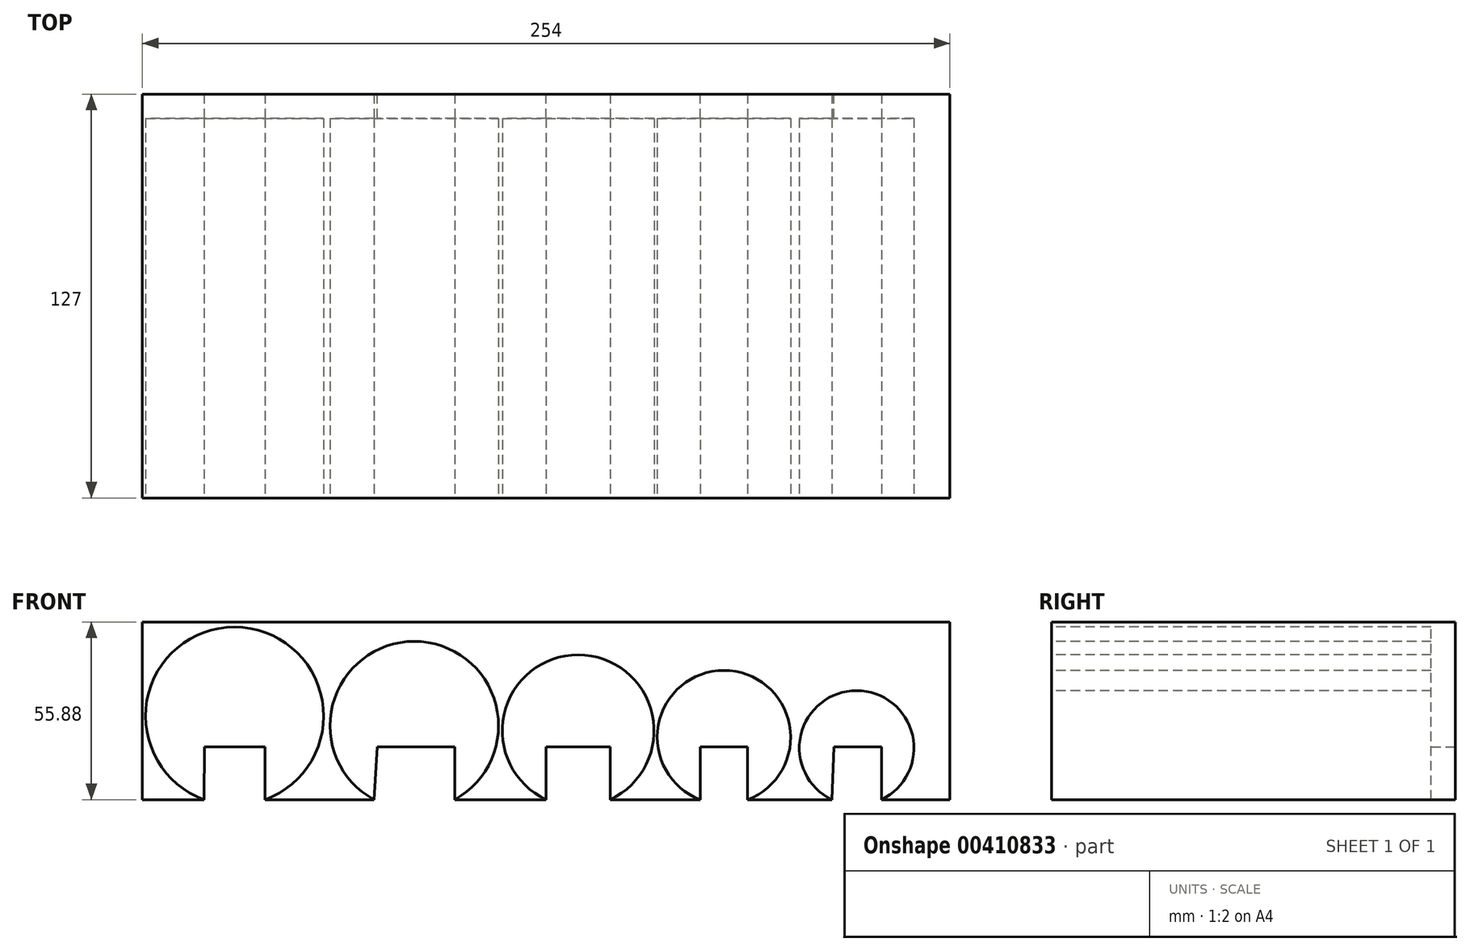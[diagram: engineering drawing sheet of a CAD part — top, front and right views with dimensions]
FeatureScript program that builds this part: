
annotation { "Feature Type Name" : "Feature", "Feature Type Description" : "" }
export const myFeature = defineFeature(function(context is Context, id is Id, definition is map)
    precondition{}
    {
        {
            var Q0;
            Q0=qCreatedBy(makeId("Front.planeOp"),FACE);
            var sketch = newSketch(context, id + "F0", { "sketchPlane" : qUnion([Q0])});
            skLineSegment(sketch, "E0.bottom", {"start": v(-127, 27.94) * mm, "end": v(127, 27.94) * mm});
            skLineSegment(sketch, "E0.top", {"start": v(-127, -27.94) * mm, "end": v(127, -27.94) * mm});
            skLineSegment(sketch, "E0.left", {"start": v(-127, 27.94) * mm, "end": v(-127, -27.94) * mm});
            skLineSegment(sketch, "E0.right", {"start": v(127, 27.94) * mm, "end": v(127, -27.94) * mm});
            skPoint(sketch, "E0.middle", {"position": v(0, 0) * mm});
            skSolve(sketch);
        }
        {
            var Q0;
            Q0=makeQuery(id+"F0.imprint","IMPRINT",FACE,{"disambiguationData":[TD([[makeQuery(id+"F0.imprint","IMPRINT",EDGE,{"derivedFrom":sQuery(id+"F0.wireOp",EDGE,"E0.bottom")}),-1.0]])]});
            extrude(context, id + "F1", {"entities" : qUnion([Q0]), "depth" : 127 * mm});
        }
        {
            var Q0;
            Q0=makeQuery(id+"F1.opExtrude","CAP_FACE",FACE,{"disambiguationData":[OSD([sQuery(id+"F0.wireOp",EDGE,"E0.bottom"),sQuery(id+"F0.wireOp",EDGE,"E0.top"),sQuery(id+"F0.wireOp",EDGE,"E0.left"),sQuery(id+"F0.wireOp",EDGE,"E0.right")])],"isStart":false});
            var sketch = newSketch(context, id + "F2", { "sketchPlane" : qUnion([Q0])});
            skArc(sketch, "E1", {"start": v(-88.41, -27.94) * mm, "mid": v(-98, 26.37) * mm, "end": v(-107.6, -27.94) * mm});
            skLineSegment(sketch, "E2.0", {"start": v(-127, -27.94) * mm, "end": v(127, -27.94) * mm});
            skSolve(sketch);
        }
        {
            var Q0;
            {var subQ2=sQuery(id+"F2.wireOp",EDGE,"E1");Q0=makeQuery(id+"F2.imprint","IMPRINT",FACE,{"disambiguationData":[TD([[makeQuery(id+"F2.imprint","IMPRINT",EDGE,{"derivedFrom":subQ2}),-1.0]])]});}
            var sketch = newSketch(context, id + "F3", { "sketchPlane" : qUnion([Q0])});
            skLineSegment(sketch, "E3.0", {"start": v(-127, -27.94) * mm, "end": v(127, -27.94) * mm});
            skArc(sketch, "E4", {"start": v(-28.8, -27.94) * mm, "mid": v(-41.48, 21.83) * mm, "end": v(-54.17, -27.94) * mm});
            skSolve(sketch);
        }
        {
            var Q0;
            {var subQ2=sQuery(id+"F2.wireOp",EDGE,"E1");Q0=makeQuery(id+"F2.imprint","IMPRINT",FACE,{"disambiguationData":[TD([[makeQuery(id+"F2.imprint","IMPRINT",EDGE,{"derivedFrom":subQ2}),-1.0]])]});}
            var sketch = newSketch(context, id + "F4", { "sketchPlane" : qUnion([Q0])});
            skLineSegment(sketch, "E5.0", {"start": v(-127, -27.94) * mm, "end": v(127, -27.94) * mm});
            skArc(sketch, "E6", {"start": v(20.14, -27.94) * mm, "mid": v(10.07, 17.6) * mm, "end": v(0, -27.94) * mm});
            skSolve(sketch);
        }
        {
            var Q0;
            {var subQ2=sQuery(id+"F2.wireOp",EDGE,"E1");Q0=makeQuery(id+"F2.imprint","IMPRINT",FACE,{"disambiguationData":[TD([[makeQuery(id+"F2.imprint","IMPRINT",EDGE,{"derivedFrom":subQ2}),-1.0]])]});}
            var sketch = newSketch(context, id + "F5", { "sketchPlane" : qUnion([Q0])});
            skLineSegment(sketch, "E7.0", {"start": v(-127, -27.94) * mm, "end": v(127, -27.94) * mm});
            skArc(sketch, "E8", {"start": v(63.36, -27.94) * mm, "mid": v(55.92, 12.7) * mm, "end": v(48.5, -27.94) * mm});
            skSolve(sketch);
        }
        {
            var Q0;
            {var subQ2=sQuery(id+"F2.wireOp",EDGE,"E1");Q0=makeQuery(id+"F2.imprint","IMPRINT",FACE,{"disambiguationData":[TD([[makeQuery(id+"F2.imprint","IMPRINT",EDGE,{"derivedFrom":subQ2}),-1.0]])]});}
            var sketch = newSketch(context, id + "F6", { "sketchPlane" : qUnion([Q0])});
            skLineSegment(sketch, "E9.0", {"start": v(-127, -27.94) * mm, "end": v(127, -27.94) * mm});
            skArc(sketch, "E10", {"start": v(105.44, -27.94) * mm, "mid": v(97.67, 6.36) * mm, "end": v(89.9, -27.94) * mm});
            skSolve(sketch);
        }
        {
            var Q0;
            {var subQ0=sQuery(id+"F6.wireOp",EDGE,"E10");Q0=makeQuery(id+"F6.imprint","IMPRINT",FACE,{"disambiguationData":[TD([[makeQuery(id+"F6.imprint","IMPRINT",EDGE,{"derivedFrom":subQ0}),1.0]])]});}
            extrude(context, id + "F7", {"entities" : qUnion([Q0]), "operationType" : NewBodyOperationType.REMOVE, "oppositeDirection" : true, "depth" : 251.46 * mm});
        }
        {
            var Q0;
            {var subQ0=sQuery(id+"F5.wireOp",EDGE,"E8");Q0=makeQuery(id+"F5.imprint","IMPRINT",FACE,{"disambiguationData":[TD([[makeQuery(id+"F5.imprint","IMPRINT",EDGE,{"derivedFrom":subQ0}),1.0]])]});}
            extrude(context, id + "F8", {"entities" : qUnion([Q0]), "operationType" : NewBodyOperationType.REMOVE, "oppositeDirection" : true, "depth" : 251.46 * mm});
        }
        {
            var Q0;
            {var subQ0=sQuery(id+"F4.wireOp",EDGE,"E6");Q0=makeQuery(id+"F4.imprint","IMPRINT",FACE,{"disambiguationData":[TD([[makeQuery(id+"F4.imprint","IMPRINT",EDGE,{"derivedFrom":subQ0}),1.0]])]});}
            extrude(context, id + "F9", {"entities" : qUnion([Q0]), "operationType" : NewBodyOperationType.REMOVE, "oppositeDirection" : true, "depth" : 251.46 * mm});
        }
        {
            var Q0;
            {var subQ0=sQuery(id+"F3.wireOp",EDGE,"E4");Q0=makeQuery(id+"F3.imprint","IMPRINT",FACE,{"disambiguationData":[TD([[makeQuery(id+"F3.imprint","IMPRINT",EDGE,{"derivedFrom":subQ0}),1.0]])]});}
            extrude(context, id + "F10", {"entities" : qUnion([Q0]), "operationType" : NewBodyOperationType.REMOVE, "oppositeDirection" : true, "depth" : 251.46 * mm});
        }
        {
            var Q0;
            {var subQ0=sQuery(id+"F2.wireOp",EDGE,"E1");Q0=makeQuery(id+"F2.imprint","IMPRINT",FACE,{"disambiguationData":[TD([[makeQuery(id+"F2.imprint","IMPRINT",EDGE,{"derivedFrom":subQ0}),1.0]])]});}
            extrude(context, id + "F11", {"entities" : qUnion([Q0]), "operationType" : NewBodyOperationType.REMOVE, "oppositeDirection" : true, "depth" : 251.46 * mm});
        }
        {
            var Q0;
            Q0=makeQuery(id+"F1.opExtrude","SWEPT_FACE",FACE,{"disambiguationData":[OSD([sQuery(id+"F0.wireOp",EDGE,"E0.top")])]});
            var sketch = newSketch(context, id + "F12", { "sketchPlane" : qUnion([Q0])});
            skLineSegment(sketch, "E11.0.0", {"start": v(-126, 127) * mm, "end": v(-70, 127) * mm});
            skLineSegment(sketch, "E11.0.1", {"start": v(-107.6, 127) * mm, "end": v(-107.6, 2.54) * mm});
            skLineSegment(sketch, "E11.0.2", {"start": v(-70, 2.54) * mm, "end": v(-126, 2.54) * mm});
            skLineSegment(sketch, "E11.0.3", {"start": v(-88.41, 2.54) * mm, "end": v(-88.41, 127) * mm});
            skLineSegment(sketch, "E12", {"start": v(-126, 4.34) * mm, "end": v(-70, 4.34) * mm});
            skLineSegment(sketch, "E13", {"start": v(-126, 2.54) * mm, "end": v(-126, 4.34) * mm});
            skLineSegment(sketch, "E14.0.0", {"start": v(79.64, 127) * mm, "end": v(115.7, 127) * mm});
            skLineSegment(sketch, "E14.0.1", {"start": v(89.9, 127) * mm, "end": v(89.9, 2.54) * mm});
            skLineSegment(sketch, "E14.0.2", {"start": v(115.7, 2.54) * mm, "end": v(79.64, 2.54) * mm});
            skLineSegment(sketch, "E14.0.3", {"start": v(105.44, 2.54) * mm, "end": v(105.44, 127) * mm});
            skLineSegment(sketch, "E15", {"start": v(-70, 4.34) * mm, "end": v(115.7, 4.34) * mm});
            skLineSegment(sketch, "E16", {"start": v(115.7, 4.34) * mm, "end": v(115.7, 2.54) * mm});
            skLineSegment(sketch, "E17", {"start": v(-70, 2.54) * mm, "end": v(79.64, 2.54) * mm});
            skSolve(sketch);
        }
        {
            var Q0;
            {var subQ5=sQuery(id+"F12.wireOp",EDGE,"E13");Q0=makeQuery(id+"F12.imprint","IMPRINT",FACE,{"disambiguationData":[TD([[makeQuery(id+"F12.imprint","IMPRINT",EDGE,{"derivedFrom":subQ5}),-1.0]])]});}
            var Q1;
            {var subQ7=sQuery(id+"F12.wireOp",EDGE,"E11.0.3");var subQ9=sQuery(id+"F12.wireOp",EDGE,"E17");var subQ11=sQuery(id+"F12.wireOp",EDGE,"E11.0.2");var subQ12=makeQuery(id+"F12.imprint","INTERSECT",VERTEX,{"derivedFrom":[subQ11,subQ9]});var subQ13=makeQuery(id+"F12.imprint","INTERSECT",VERTEX,{"derivedFrom":[subQ11,subQ7]});Q1=makeQuery(id+"F12.imprint","IMPRINT",FACE,{"disambiguationData":[TD([[makeQuery(id+"F12.imprint","IMPRINT",EDGE,{"disambiguationData":[TD([[subQ13,1.0],[subQ12,-1.0]])],"derivedFrom":subQ11}),-1.0]])]});}
            var Q2;
            {var subQ0=sQuery(id+"F12.wireOp",EDGE,"E15");var subQ1=sQuery(id+"F3.wireOp",EDGE,"E4");var subQ2=sQuery(id+"F3.wireOp",EDGE,"E3.0");var subQ3=makeQuery(id+"F10.boolean.opBoolean","COPY",EDGE,{"derivedFrom":makeQuery(id+"F10.opExtrude","SWEPT_EDGE",EDGE,{"disambiguationData":[OSD([subQ2,subQ1]),TDD([makeQuery(id+"F3.imprint","INTERSECT",VERTEX,{"disambiguationData":[OD(0.0)],"derivedFrom":[subQ2,subQ1]})])]})});var subQ4=makeQuery(id+"F12.imprint","INTERSECT",VERTEX,{"derivedFrom":[subQ3,subQ0]});Q2=makeQuery(id+"F12.imprint","IMPRINT",FACE,{"disambiguationData":[TD([[makeQuery(id+"F12.imprint","IMPRINT",EDGE,{"disambiguationData":[TD([[subQ4,-1.0]])],"derivedFrom":subQ0}),-1.0]])]});}
            var Q3;
            {var subQ0=sQuery(id+"F12.wireOp",EDGE,"E15");var subQ1=sQuery(id+"F4.wireOp",EDGE,"E6");var subQ2=sQuery(id+"F4.wireOp",EDGE,"E5.0");var subQ3=makeQuery(id+"F9.boolean.opBoolean","COPY",EDGE,{"derivedFrom":makeQuery(id+"F9.opExtrude","SWEPT_EDGE",EDGE,{"disambiguationData":[OSD([subQ2,subQ1]),TDD([makeQuery(id+"F4.imprint","INTERSECT",VERTEX,{"disambiguationData":[OD(0.0)],"derivedFrom":[subQ2,subQ1]})])]})});var subQ4=makeQuery(id+"F12.imprint","INTERSECT",VERTEX,{"derivedFrom":[subQ3,subQ0]});Q3=makeQuery(id+"F12.imprint","IMPRINT",FACE,{"disambiguationData":[TD([[makeQuery(id+"F12.imprint","IMPRINT",EDGE,{"disambiguationData":[TD([[subQ4,-1.0]])],"derivedFrom":subQ0}),-1.0]])]});}
            var Q4;
            {var subQ5=sQuery(id+"F12.wireOp",EDGE,"E14.0.2");var subQ8=sQuery(id+"F12.wireOp",EDGE,"E14.0.1");var subQ11=makeQuery(id+"F12.imprint","INTERSECT",VERTEX,{"derivedFrom":[subQ8,subQ5]});Q4=makeQuery(id+"F12.imprint","IMPRINT",FACE,{"disambiguationData":[TD([[makeQuery(id+"F12.imprint","IMPRINT",EDGE,{"disambiguationData":[TD([[subQ11,-1.0]])],"derivedFrom":subQ8}),1.0]])]});}
            var Q5;
            {var subQ3=sQuery(id+"F12.wireOp",EDGE,"E16");Q5=makeQuery(id+"F12.imprint","IMPRINT",FACE,{"disambiguationData":[TD([[makeQuery(id+"F12.imprint","IMPRINT",EDGE,{"derivedFrom":subQ3}),-1.0]])]});}
            extrude(context, id + "F13", {"entities" : qUnion([Q0, Q1, Q2, Q3, Q4, Q5]), "operationType" : NewBodyOperationType.REMOVE, "oppositeDirection" : true, "depth" : 28.7 * mm});
        }
        {
            var Q0;
            Q0=makeQuery(id+"F1.opExtrude","CAP_FACE",FACE,{"disambiguationData":[OSD([sQuery(id+"F0.wireOp",EDGE,"E0.bottom"),sQuery(id+"F0.wireOp",EDGE,"E0.top"),sQuery(id+"F0.wireOp",EDGE,"E0.left"),sQuery(id+"F0.wireOp",EDGE,"E0.right")])],"isStart":true});
            var sketch = newSketch(context, id + "F14", { "sketchPlane" : qUnion([Q0])});
            skLineSegment(sketch, "E18", {"start": v(107.5, -27.94) * mm, "end": v(107.5, 0) * mm});
            skLineSegment(sketch, "E19", {"start": v(107.5, 0) * mm, "end": v(90.55, 0) * mm});
            skLineSegment(sketch, "E20", {"start": v(90.55, 0) * mm, "end": v(90.55, -27.94) * mm});
            skLineSegment(sketch, "E21", {"start": v(90.55, -27.94) * mm, "end": v(107.5, -27.94) * mm});
            skLineSegment(sketch, "E22", {"start": v(51.66, -27.94) * mm, "end": v(51.66, 0) * mm});
            skLineSegment(sketch, "E23", {"start": v(51.66, 0) * mm, "end": v(30.15, 0) * mm});
            skLineSegment(sketch, "E24", {"start": v(30.15, 0) * mm, "end": v(30.15, -27.94) * mm});
            skLineSegment(sketch, "E25", {"start": v(30.15, -27.94) * mm, "end": v(51.66, -27.94) * mm});
            skLineSegment(sketch, "E26", {"start": v(-116.22, -27.94) * mm, "end": v(0, 0) * mm});
            skLineSegment(sketch, "E27", {"start": v(0, 0) * mm, "end": v(-18.74, 0) * mm});
            skLineSegment(sketch, "E28", {"start": v(-18.74, 0) * mm, "end": v(-18.74, -27.94) * mm});
            skLineSegment(sketch, "E29", {"start": v(-116.22, -27.94) * mm, "end": v(-18.74, -27.94) * mm});
            skLineSegment(sketch, "E30", {"start": v(-48.84, -27.94) * mm, "end": v(-48.84, 0) * mm});
            skLineSegment(sketch, "E31", {"start": v(-48.84, 0) * mm, "end": v(-63.66, 0) * mm});
            skLineSegment(sketch, "E32", {"start": v(-63.66, 0) * mm, "end": v(-63.66, -27.94) * mm});
            skLineSegment(sketch, "E33", {"start": v(-63.66, -27.94) * mm, "end": v(-48.84, -27.94) * mm});
            skLineSegment(sketch, "E34", {"start": v(-91.1, -27.94) * mm, "end": v(-91.1, 0) * mm});
            skLineSegment(sketch, "E35", {"start": v(-91.1, 0) * mm, "end": v(-104.6, 0) * mm});
            skLineSegment(sketch, "E36", {"start": v(-104.6, 0) * mm, "end": v(-104.6, -27.94) * mm});
            skLineSegment(sketch, "E37", {"start": v(-104.6, -27.94) * mm, "end": v(-91.1, -27.94) * mm});
            skSolve(sketch);
        }
        {
            var Q0;
            Q0=makeQuery(id+"F14.imprint","IMPRINT",FACE,{"disambiguationData":[TD([[makeQuery(id+"F14.imprint","IMPRINT",EDGE,{"derivedFrom":sQuery(id+"F14.wireOp",EDGE,"E34")}),1.0]])]});
            var Q1;
            Q1=makeQuery(id+"F14.imprint","IMPRINT",FACE,{"disambiguationData":[TD([[makeQuery(id+"F14.imprint","IMPRINT",EDGE,{"derivedFrom":sQuery(id+"F14.wireOp",EDGE,"E30")}),1.0]])]});
            var Q2;
            Q2=makeQuery(id+"F14.imprint","IMPRINT",FACE,{"disambiguationData":[TD([[makeQuery(id+"F14.imprint","IMPRINT",EDGE,{"derivedFrom":sQuery(id+"F14.wireOp",EDGE,"E26")}),1.0]])]});
            var Q3;
            Q3=makeQuery(id+"F14.imprint","IMPRINT",FACE,{"disambiguationData":[TD([[makeQuery(id+"F14.imprint","IMPRINT",EDGE,{"derivedFrom":sQuery(id+"F14.wireOp",EDGE,"E22")}),1.0]])]});
            var Q4;
            Q4=makeQuery(id+"F14.imprint","IMPRINT",FACE,{"disambiguationData":[TD([[makeQuery(id+"F14.imprint","IMPRINT",EDGE,{"derivedFrom":sQuery(id+"F14.wireOp",EDGE,"E18")}),1.0]])]});
            extrude(context, id + "F15", {"entities" : qUnion([Q0, Q1, Q2, Q3, Q4]), "operationType" : NewBodyOperationType.REMOVE, "oppositeDirection" : true, "depth" : 76.2 * mm});
        }
        {
            var Q0;
            Q0=makeQuery(id+"F1.opExtrude","CAP_FACE",FACE,{"disambiguationData":[OSD([sQuery(id+"F0.wireOp",EDGE,"E0.bottom"),sQuery(id+"F0.wireOp",EDGE,"E0.top"),sQuery(id+"F0.wireOp",EDGE,"E0.left"),sQuery(id+"F0.wireOp",EDGE,"E0.right")])],"isStart":true});
            var sketch = newSketch(context, id + "F16", { "sketchPlane" : qUnion([Q0])});
            skLineSegment(sketch, "E38", {"start": v(-127, 27.94) * mm, "end": v(-127, -27.94) * mm});
            skLineSegment(sketch, "E39", {"start": v(-127, -27.94) * mm, "end": v(-105.44, -27.94) * mm});
            skLineSegment(sketch, "E40", {"start": v(-105.44, -27.94) * mm, "end": v(-105.44, -11.35) * mm});
            skLineSegment(sketch, "E41", {"start": v(-105.44, -11.35) * mm, "end": v(-90.53, -11.35) * mm});
            skLineSegment(sketch, "E42", {"start": v(-90.53, -11.35) * mm, "end": v(-89.9, -27.94) * mm});
            skLineSegment(sketch, "E43", {"start": v(-89.9, -27.94) * mm, "end": v(-63.36, -27.94) * mm});
            skLineSegment(sketch, "E44", {"start": v(-63.36, -27.94) * mm, "end": v(-63.36, -11.35) * mm});
            skLineSegment(sketch, "E45", {"start": v(-63.36, -11.35) * mm, "end": v(-48.5, -11.35) * mm});
            skLineSegment(sketch, "E46", {"start": v(-48.5, -11.35) * mm, "end": v(-48.5, -27.94) * mm});
            skLineSegment(sketch, "E47", {"start": v(-20.14, -27.94) * mm, "end": v(-20.14, -11.35) * mm});
            skLineSegment(sketch, "E48", {"start": v(-20.14, -11.35) * mm, "end": v(0, -11.35) * mm});
            skLineSegment(sketch, "E49", {"start": v(0, -11.35) * mm, "end": v(0, -27.94) * mm});
            skLineSegment(sketch, "E50", {"start": v(0, -27.94) * mm, "end": v(28.8, -27.94) * mm});
            skLineSegment(sketch, "E51", {"start": v(28.8, -27.94) * mm, "end": v(28.8, -11.35) * mm});
            skLineSegment(sketch, "E52", {"start": v(28.8, -11.35) * mm, "end": v(53.17, -11.35) * mm});
            skLineSegment(sketch, "E53", {"start": v(54.17, -27.94) * mm, "end": v(53.17, -11.35) * mm});
            skLineSegment(sketch, "E54", {"start": v(88.41, -27.94) * mm, "end": v(88.41, -11.35) * mm});
            skLineSegment(sketch, "E55", {"start": v(88.41, -11.35) * mm, "end": v(107.43, -11.35) * mm});
            skLineSegment(sketch, "E56", {"start": v(107.43, -11.35) * mm, "end": v(107.6, -27.94) * mm});
            skLineSegment(sketch, "E57", {"start": v(54.17, -27.94) * mm, "end": v(88.41, -27.94) * mm});
            skLineSegment(sketch, "E58", {"start": v(107.6, -27.94) * mm, "end": v(127, -27.94) * mm});
            skLineSegment(sketch, "E59", {"start": v(127, -27.94) * mm, "end": v(127, 27.94) * mm});
            skLineSegment(sketch, "E60", {"start": v(127, 27.94) * mm, "end": v(-127, 27.94) * mm});
            skLineSegment(sketch, "E61", {"start": v(-48.5, -27.94) * mm, "end": v(-20.14, -27.94) * mm});
            skSolve(sketch);
        }
        {
            var Q0;
            Q0 = qSketchRegion(id + "F16", true);
            extrude(context, id + "F17", {"entities" : qUnion([Q0]), "operationType" : NewBodyOperationType.ADD, "oppositeDirection" : true, "depth" : 7.62 * mm});
        }
    });
